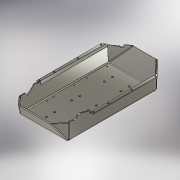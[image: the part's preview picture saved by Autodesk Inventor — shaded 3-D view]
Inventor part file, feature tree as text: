
AUTODESK INVENTOR PART (.ipt)
format: ipt  version: 2017.3 (Build 213256000, 256)  size: 1,775,616 bytes
history: native  units: mm
features: sheet_metal_op x51, other x25, sketch x22, plane x18, hole x2, mirror x1
ambient origin geometry x8: Origin, YZ Plane, XZ Plane, XY Plane, X Axis, Y Axis, Z Axis, Center Point
bodies: Solid1 (feature_tree)
feature tree (119):
  sheet_metal_op  "Face1"
  sheet_metal_op  "Flange1"
  sheet_metal_op  "Flange2"
  sheet_metal_op  "Flange3"
  sheet_metal_op  "Flange4"
  plane  "Work Plane1"
  sheet_metal_op  "Flange5"
  sheet_metal_op  "Unfold1"
  sheet_metal_op  "Refold1"
  sheet_metal_op  "Unfold2"
  plane  "Work Plane2"
  sheet_metal_op  "Face2"
  sheet_metal_op  "Refold2"
  sheet_metal_op  "Fold40"
  plane  "Work Plane4"
  sketch  "Sketch14"  dims[d2=4.763mm d3=4.763mm]
  plane  "Work Plane3"
  plane  "Work Plane20"
  sketch  "Sketch50"  dims[d5=9.526mm]
  sheet_metal_op  "Unfold6"
  plane  "Work Plane10"
  sheet_metal_op  "Face5"
  sheet_metal_op  "Refold6"
  sheet_metal_op  "Fold41"
  plane  "Work Plane7"
  sheet_metal_op  "Flange6"
  other  "MID-PLANE2"
  sketch  "Sketch66"  dims[d10=19.052mm]
  plane  "Work Plane8"
  sheet_metal_op  "Unfold4"
  sheet_metal_op  "Refold4"
  sheet_metal_op  "Unfold8"
  plane  "Work Plane23"
  sheet_metal_op  "Face9"
  sheet_metal_op  "Refold8"
  sheet_metal_op  "Fold42"
  sheet_metal_op  "Unfold9"
  plane  "Work Plane24"
  sheet_metal_op  "Face10"
  sheet_metal_op  "Refold9"
  sheet_metal_op  "Fold43"
  other  "MID-PLANE3"
  sketch  "Sketch73"  dims[d16=4.763mm]
  plane  "Work Plane25"
  mirror  "Mirror2"
  plane  "Work Plane30"
  sheet_metal_op  "Flange9"
  plane  "Work Plane27"
  hole  "Hole2"  [1 undecoded]
  plane  "Work Plane28"
  sheet_metal_op  "Flange10"
  plane  "Work Plane29"
  plane  "Work Plane31"
  sheet_metal_op  "Unfold11"
  plane  "Work Plane32"
  sheet_metal_op  "Refold10"
  plane  "Work Plane33"
  hole  "Hole3"  [1 undecoded]
  sketch  "Sketch1"  dims[d0=259.554mm d1=463.55mm]
  other  "Plate1"
  other  "Plate2"
  sheet_metal_op  "Bend1"
  sheet_metal_op  "Corner1"
  other  "Plate3"
  sheet_metal_op  "Bend2"
  sheet_metal_op  "Corner2"
  other  "Plate4"
  sheet_metal_op  "Bend3"
  sheet_metal_op  "Corner3"
  other  "Plate5"
  sheet_metal_op  "Bend4"
  sheet_metal_op  "Corner4"
  other  "Plate6"
  sheet_metal_op  "Bend5"
  sheet_metal_op  "Corner5"
  other  "Plate7"
  sheet_metal_op  "Bend6"
  other  "Plate9"
  sheet_metal_op  "Bend8"
  sheet_metal_op  "Corner6"
  sketch  "Sketch22"  dims[d4=2.3815mm]
  other  "Plate11"
  sheet_metal_op  "Bend10"
  sketch  "Sketch64"  dims[d6=4.763mm]
  sketch  "Sketch65"  dims[d7=87.1798mm d8=15.280358mm d9=4.763mm]
  sketch  "Sketch68"  dims[d11=4.763mm]
  other  "Plate17"
  sheet_metal_op  "Bend16"
  sketch  "Sketch69"  dims[d12=6.0mm]
  sketch  "Sketch70"  dims[d13=4.763mm]
  other  "Plate18"
  sheet_metal_op  "Bend17"
  sketch  "Sketch71"  dims[d14=2.3815mm]
  sketch  "Sketch72"  dims[d15=9.526mm]
  sketch  "Sketch74"  dims[d17=21.827mm d18=15.280358mm d19=4.763mm]
  other  "Plate19"
  sheet_metal_op  "Bend18"
  sheet_metal_op  "Corner9"
  sketch  "Sketch75"  dims[d20=19.052mm]
  sketch  "Sketch76"  dims[d21=4.763mm]
  sketch  "Sketch77"  dims[d22=6.0mm]
  other  "Plate20"
  sheet_metal_op  "Bend19"
  sheet_metal_op  "Corner10"
  sketch  "Sketch78"  dims[d23=4.763mm]
  sketch  "Sketch79"  dims[d24=2.3815mm]
  sketch  "Sketch80"  dims[d25=9.526mm]
  sketch  "Sketch81"  dims[d26=4.763mm]
  sketch  "Sketch82"  dims[d27=87.1798mm d28=15.280358mm d29=4.763mm d30=19.052mm d31=4.763mm d32=6.0mm d33=4.763mm d34=2.3815mm d35=9.526mm d36=4.763mm d37=21.827mm d38=15.280358mm d39=4.763mm d40=19.052mm d41=4.763mm d42=6.0mm d43=0.0mm d75=4.763mm d76=2.3815mm d77=9.526mm d78=4.763mm d79=99.15mm d80=10.268191mm d81=4.763mm d82=19.052mm d83=4.763mm d84=6.0mm d118=4.763mm d119=0.0mm d120=0.0mm d146=4.763mm d147=12.0mm d148=6.0mm d149=9.526mm d150=4.763mm d195=0.0mm d223=0.0mm d228=4.232488mm d480=0.0mm d485=4.763mm d486=2.3815mm d487=9.526mm d488=4.763mm d489=104.002mm d490=8.203047mm d491=4.763mm d492=19.052mm d493=4.763mm d494=6.0mm d495=0.0mm d501=4.763mm d502=0.0mm d608=0.0mm d642=4.763mm d643=4.763mm d644=2.3815mm d645=9.526mm d646=4.763mm d677=1.0mm d684=1.0mm d781=5.585054mm d783=1.0mm d784=63.399439mm d809=3.9mm d909=108.0mm d910=0.0mm d959=125.0mm d960=125.0mm d964=287.0mm d965=285.0mm d970=286.0mm d971=287.0mm d974=19.0mm d988=90.0deg d989=6.0mm d994=35.0mm d1000=0.0mm d1001=108.0mm d1038=87.303716mm d1302=5.472384mm d1303=5.455996mm d1305=10.663185mm d1317=4.232423mm d1403=0.0mm d1456=4.272566mm d1586=8.272777mm d1589=8.349655mm d1590=24.057618mm d1592=4.18879mm d1597=4.18879mm d1621=8.388766mm d1622=23.98074mm d1623=23.896599mm d1624=16.873813mm d1625=7.022786mm d1626=8.188636mm d1629=3.991568mm d1633=3.991568mm d1634=11.716395mm d1748=22.5deg d1753=1.0mm d1754=1.0mm d1755=22.5deg d1756=22.5deg d1757=39.844461mm d1758=4.232423mm d1759=11.47554mm d1760=67.5deg d1761=81.805409mm d1763=94.778826mm d1768=94.778826mm d1770=22.5deg d1775=1.0mm d1779=54.0mm d1780=53.999998mm d1796=101.50547mm d1797=90.0deg d1798=8.0mm d1855=0.079716mm d1856=0.048568mm d1860=6.9mm d1867=28.769135mm d1892=77.306551mm d1893=64.134985mm d1904=22.5deg d1905=1.0mm d1906=81.805409mm d1907=39.844461mm d1910=67.5deg d1911=81.805409mm d1914=90.0deg d1915=3.9mm d1916=4.763mm d1917=2.3815mm d1918=9.526mm d1919=4.763mm d1920=9.512044mm d1921=4.763mm d1922=90.0deg d1923=8.0mm d1925=6.9mm d1926=101.50547mm d1927=28.769135mm d1933=81.805409mm d1934=64.135mm d1935=77.306551mm d1941=90.0deg d1942=3.9mm d1943=4.763mm d1944=2.3815mm d1945=9.526mm d1946=4.763mm d1947=9.512044mm d1948=4.763mm d1949=0.0mm d1952=74.0mm d1958=73.0mm d1959=73.0mm d1960=1.527954mm d1963=79.310386mm d1964=1.0mm d1966=5.585054mm d1967=1.0mm d1968=58.250431mm d1969=58.250431mm d1970=63.399439mm d1988=0.0mm d1995=10.0mm d2004=94.14mm d2008=7.673392mm d2009=28.831967mm d2010=4.763mm d2011=4.763mm d2012=2.3815mm d2013=9.526mm d2014=4.763mm d2015=90.0deg d2016=3.9mm d2020=4.763mm d2021=2.3815mm d2022=9.526mm d2023=4.763mm d2024=10.12291mm d2025=4.763mm d2030=75.790976mm d2031=58.250431mm d2032=58.250431mm d2033=0.0mm d2034=90.0deg d2035=10.0mm d2036=7.673mm d2037=28.832839mm d2038=94.14mm d2039=4.763mm d2040=4.763mm d2041=2.3815mm d2042=9.526mm d2043=4.763mm d2044=90.0deg d2045=3.9mm d2046=4.763mm d2047=2.3815mm d2048=9.526mm d2049=4.763mm d2050=10.12291mm d2051=4.763mm d2052=0.0mm d2058=0.0mm d2059=1.174643mm d2060=40.0mm d2061=4.5mm d2062=12.0mm d2073=4.763mm d2074=0.0mm d2075=4.763mm d2076=2.3815mm d2077=9.526mm d2078=4.763mm d2079=22.0mm d2080=0.0mm d2081=4.763mm d2082=19.052mm d2083=4.763mm d2084=6.0mm d2085=0.0mm d2086=5.0mm d2087=15.0mm d2090=5.0mm d2091=17.355mm d2093=15.0mm d2094=222.0mm d2095=256.709826mm d2096=17.354826mm d2097=20.0mm d2099=109.0mm d2100=10.0mm d2102=10.0mm d2104=109.0mm d2105=17.355mm d2106=17.354826mm d2107=5.0mm d2108=160.0mm d2109=17.354826mm d2110=36.0mm d2111=5.0mm d2112=17.355mm d2113=36.0mm d2114=20.0mm d2116=109.0mm d2117=10.0mm d2119=10.0mm d2121=109.0mm d2122=5.0mm d2123=17.354826mm d2124=335.0mm d2125=66.0mm d2126=5.0mm d2127=17.355mm d2128=66.0mm d2129=20.0mm d2131=109.0mm d2132=10.0mm d2134=10.0mm d2136=109.0mm d2137=124.0mm d2138=269.0mm d2139=19.55mm d2140=5.0mm d2141=6.0mm d2142=4.0mm d2143=2.0mm d2144=90.0deg d2145=4.763mm d2146=20.594885mm d2148=0.0mm d2151=1.0mm d2152=1.0mm d2153=1.0mm d2154=4.763mm d2155=0.0mm d2156=4.763mm d2157=2.3815mm d2158=9.526mm d2159=4.763mm d2160=22.0mm d2161=0.0mm d2162=4.763mm d2163=19.052mm d2164=4.763mm d2165=6.0mm d2166=0.0mm d2167=0.0mm d2170=1.0mm d2171=1.0mm d2172=1.0mm d2173=1.0mm d2174=7.703855mm d2175=7.703855mm d2176=8.0mm d2177=0.0mm d2179=1.0mm d2180=109.99mm d2181=17.06695mm d2182=17.432156mm d2186=5.411818mm d2210=72.0mm d2225=90.0deg d2232=6.109871mm d2233=90.0deg d2239=6.108652mm d2243=195.0mm d2245=72.0mm d2247=90.0deg d2248=21.067mm d2251=42.169884mm d2253=90.0deg d2256=4.763mm d2257=0.0mm d2261=5.0mm d2270=10.0mm d2278=3.958446mm d2279=8.993074mm d2281=15.0mm d2282=0.25mm d2283=0.25mm d2284=10.0mm d2286=297.382412mm d2287=19.0mm d2296=19.0mm d2297=17.0mm d2298=15.0mm d2300=46.228436mm d2301=15.793919mm d2303=14.042693mm d2304=2.05121mm d2306=7.0mm d2308=1.0mm d2311=5.0mm d2312=10.402371mm d2313=30.501382mm d2314=5.62911mm d2316=50.0mm d2317=90.0deg d2318=7.0mm d2320=297.382412mm d2321=2.0mm d2322=0.0mm d2328=20.00995mm d2329=4.763mm d2330=0.0mm d2335=2.0mm d2336=6.0mm d2337=2.0mm d2338=6.0mm d2339=2.0mm d2340=6.0mm d2343=1.5mm d2344=78.5mm d2345=2.0mm d2346=6.0mm d2347=2.0mm d2348=6.0mm d2349=2.0mm d2350=6.0mm d2351=2.0mm d2352=6.0mm d2353=2.0mm d2354=6.0mm d2355=77.0mm d2356=4.763mm d2357=0.0mm d2358=0.025mm d2359=24.926453mm d2360=29.067mm d2361=0.0mm d2362=13.0mm d2363=13.0mm d2364=13.0mm d2365=13.0mm d2366=4.763mm d2367=0.0mm d2368=0.0mm d2369=5.0mm d2370=5.0mm d2371=88.8mm d2372=5.0mm d2373=43.0mm d2374=5.0mm d2375=43.0mm d2376=88.8mm d2377=5.0mm d2378=5.0mm d2379=43.0mm d2380=5.0mm d2381=88.8mm d2382=5.0mm d2383=43.0mm d2384=88.8mm d2385=5.0mm d2386=5.0mm d2387=43.0mm d2388=5.0mm d2389=88.8mm d2390=5.0mm d2391=43.0mm d2392=88.8mm d2393=10.0mm d2394=6.0mm d2395=4.0mm d2396=2.0mm d2397=90.0deg d2398=4.763mm d2399=20.594885mm]
  other  "Cut15"
  other  "Cut1"
  other  "Cut4"
  other  "Cut10"
  other  "Cut12"
  other  "Cut11"
  other  "Cut13"
  other  "Cut14"
  other  "Cut16"
  other  "Definition1"
note: 2 required parameter values undecoded (feature->parameter linkage not recoverable at this tier; creation-order binding heuristic only, values carry confidence <= 0.55)
